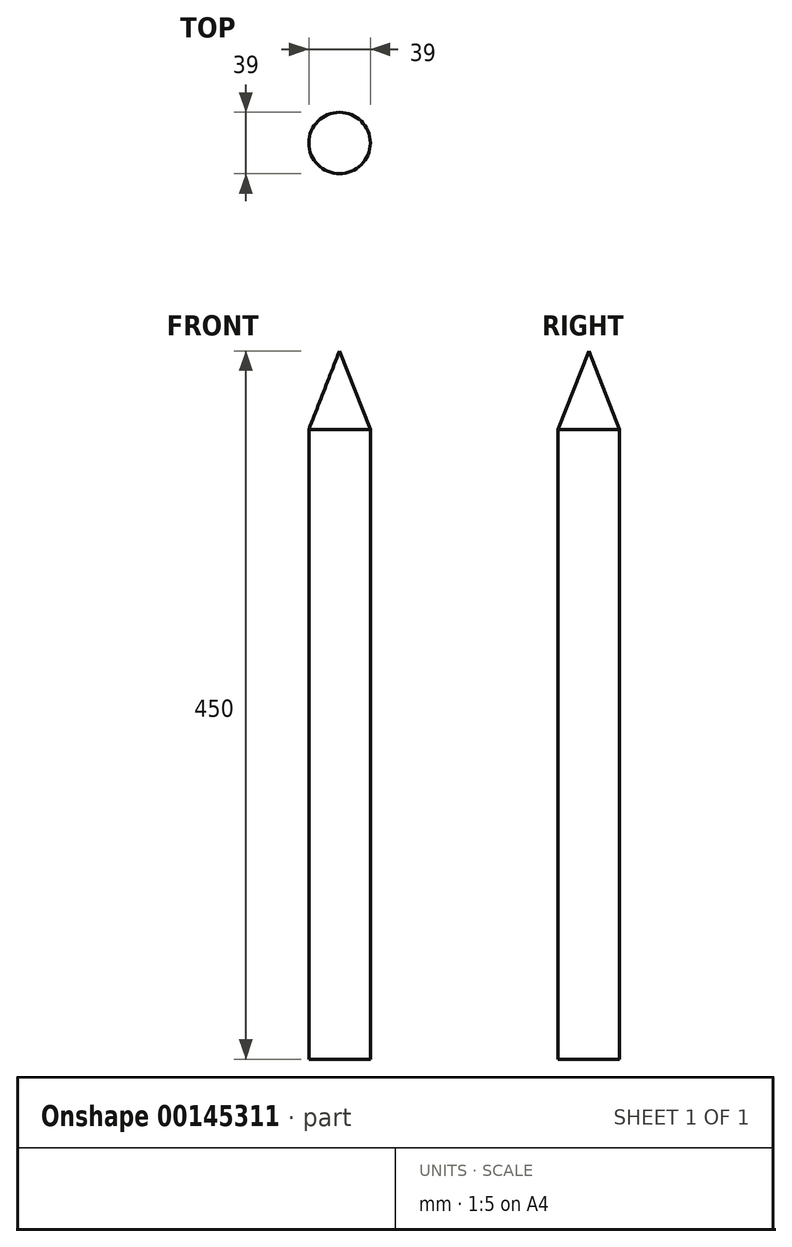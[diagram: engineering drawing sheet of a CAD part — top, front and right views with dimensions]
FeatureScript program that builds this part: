
annotation { "Feature Type Name" : "Feature", "Feature Type Description" : "" }
export const myFeature = defineFeature(function(context is Context, id is Id, definition is map)
    precondition{}
    {
        {
            var Q0;
            Q0=qCreatedBy(makeId("Front.planeOp"),FACE);
            var sketch = newSketch(context, id + "F0", { "sketchPlane" : qUnion([Q0])});
            skLineSegment(sketch, "E0.bottom", {"start": v(19.5, 200) * mm, "end": v(-19.5, 200) * mm});
            skLineSegment(sketch, "E0.top", {"start": v(19.5, -200) * mm, "end": v(-19.5, -200) * mm});
            skLineSegment(sketch, "E0.left", {"start": v(19.5, 200) * mm, "end": v(19.5, -200) * mm});
            skLineSegment(sketch, "E0.right", {"start": v(-19.5, 200) * mm, "end": v(-19.5, -200) * mm});
            skPoint(sketch, "E0.middle", {"position": v(0, 0) * mm});
            skLineSegment(sketch, "E1", {"start": v(0, 250) * mm, "end": v(-19.5, 200) * mm});
            skLineSegment(sketch, "E2", {"start": v(0, 250) * mm, "end": v(19.5, 200) * mm});
            skLineSegment(sketch, "E3", {"start": v(0, 250) * mm, "end": v(0, -200) * mm});
            skSolve(sketch);
        }
        {
            var Q0;
            {var subQ0=sQuery(id+"F0.wireOp",EDGE,"E0.left");Q0=makeQuery(id+"F0.imprint","IMPRINT",FACE,{"disambiguationData":[TD([[makeQuery(id+"F0.imprint","IMPRINT",EDGE,{"derivedFrom":subQ0}),-1.0]])]});}
            var Q1;
            {var subQ0=sQuery(id+"F0.wireOp",EDGE,"E2");Q1=makeQuery(id+"F0.imprint","IMPRINT",FACE,{"disambiguationData":[TD([[makeQuery(id+"F0.imprint","IMPRINT",EDGE,{"derivedFrom":subQ0}),-1.0]])]});}
            var Q2;
            Q2=sQuery(id+"F0.wireOp",EDGE,"E3");
            revolve(context, id + "F1", {"entities" : qUnion([Q0, Q1]), "axis" : qUnion([Q2]), "revolveType" : RevolveType.FULL});
        }
    });
